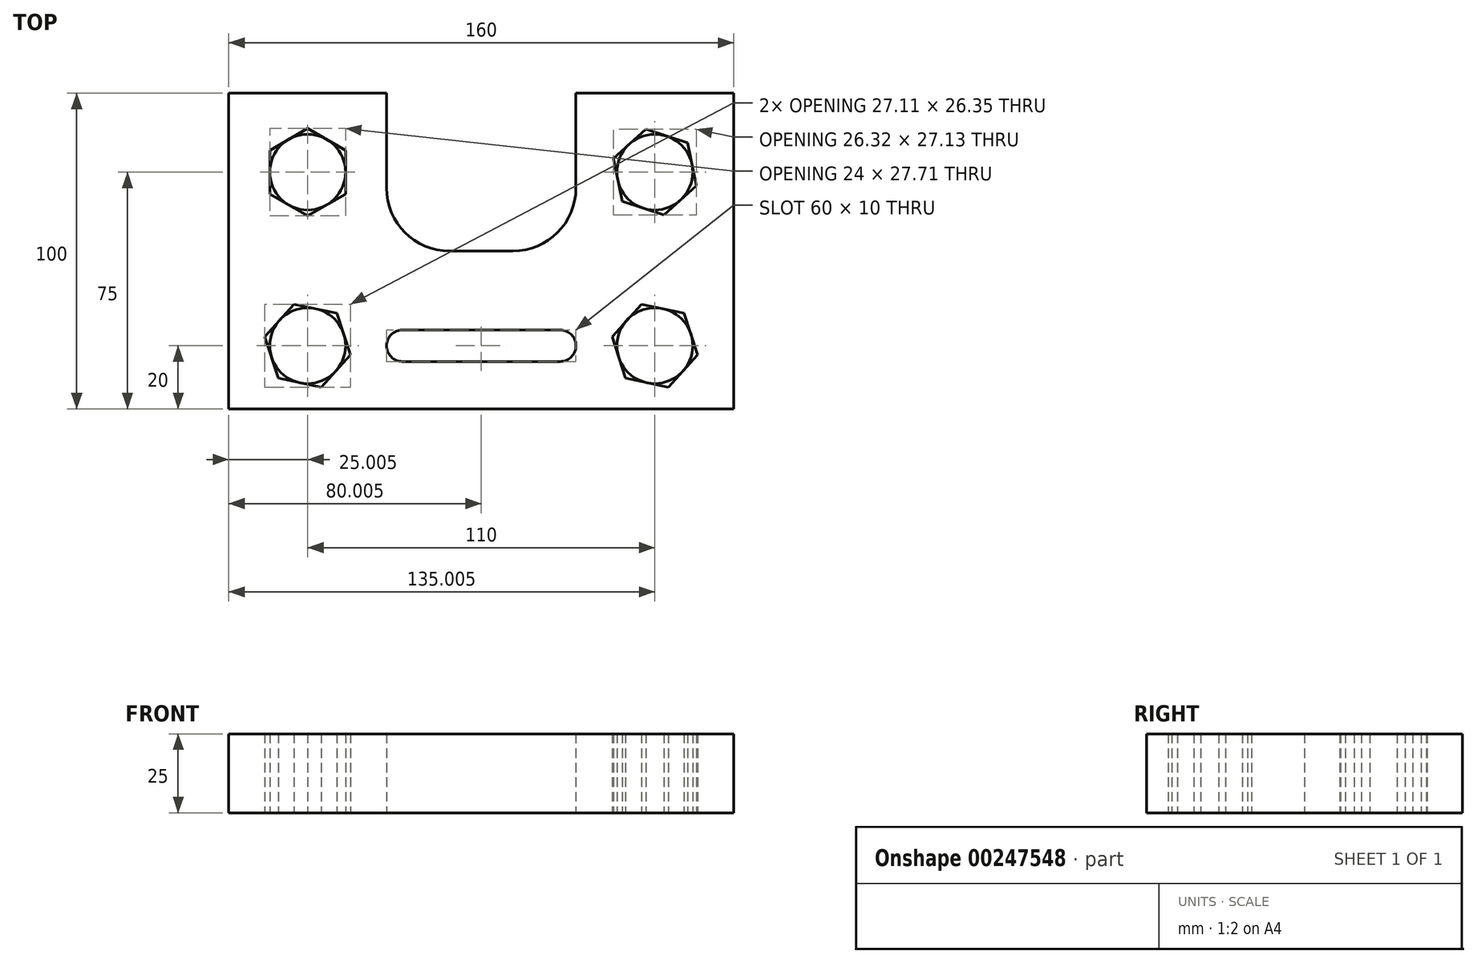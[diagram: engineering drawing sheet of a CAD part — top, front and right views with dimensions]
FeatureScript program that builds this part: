
annotation { "Feature Type Name" : "Feature", "Feature Type Description" : "" }
export const myFeature = defineFeature(function(context is Context, id is Id, definition is map)
    precondition{}
    {
        {
            var Q0;
            Q0=qCreatedBy(makeId("Top.planeOp"),FACE);
            var sketch = newSketch(context, id + "F0", { "sketchPlane" : qUnion([Q0])});
            skLineSegment(sketch, "E0", {"start": v(-28.5, -50) * mm, "end": v(21.5, -50) * mm});
            skLineSegment(sketch, "E1", {"start": v(21.5, -50) * mm, "end": v(51.5, -50) * mm});
            skLineSegment(sketch, "E2", {"start": v(51.5, -50) * mm, "end": v(76.5, -50) * mm});
            skLineSegment(sketch, "E3", {"start": v(76.5, -50) * mm, "end": v(76.5, -30) * mm});
            skLineSegment(sketch, "E4", {"start": v(76.5, -30) * mm, "end": v(76.5, 25) * mm});
            skLineSegment(sketch, "E5", {"start": v(76.5, 25) * mm, "end": v(76.5, 50) * mm});
            skLineSegment(sketch, "E6", {"start": v(76.5, 50) * mm, "end": v(26.5, 50) * mm});
            skLineSegment(sketch, "E7", {"start": v(26.5, 50) * mm, "end": v(26.5, 20) * mm});
            skLineSegment(sketch, "E8", {"start": v(6.5, 0) * mm, "end": v(-13.5, 0) * mm});
            skLineSegment(sketch, "E9", {"start": v(-33.5, 20) * mm, "end": v(-33.5, 50) * mm});
            skLineSegment(sketch, "E10", {"start": v(-33.5, 50) * mm, "end": v(-83.5, 50) * mm});
            skLineSegment(sketch, "E11", {"start": v(-83.5, -50) * mm, "end": v(-83.5, -30) * mm});
            skLineSegment(sketch, "E12", {"start": v(-83.5, -30) * mm, "end": v(-83.5, 25) * mm});
            skLineSegment(sketch, "E13", {"start": v(-83.5, 25) * mm, "end": v(-83.5, 50) * mm});
            skPoint(sketch, "E14", {"position": v(51.5, -30) * mm});
            skPoint(sketch, "E15", {"position": v(51.5, 25) * mm});
            skLineSegment(sketch, "E16", {"start": v(-83.5, -50) * mm, "end": v(-58.5, -50) * mm});
            skLineSegment(sketch, "E17", {"start": v(-58.5, -50) * mm, "end": v(-28.5, -50) * mm});
            skPoint(sketch, "E18", {"position": v(-58.5, -30) * mm});
            skPoint(sketch, "E19", {"position": v(-58.5, 25) * mm});
            skCircle(sketch, "E20", {"center": v(-58.5, 25) * mm, "radius": 12 * mm});
            skCircle(sketch, "E21", {"center": v(-58.5, -30) * mm, "radius": 12 * mm});
            skCircle(sketch, "E22", {"center": v(51.5, -30) * mm, "radius": 12 * mm});
            skCircle(sketch, "E23", {"center": v(51.5, 25) * mm, "radius": 12 * mm});
            skPoint(sketch, "E24.visualSharp", {"position": v(-33.5, 0) * mm});
            skArc(sketch, "E24.filletArc", {"start": v(-33.5, 20) * mm, "mid": v(-27.65, 5.86) * mm, "end": v(-13.5, 0) * mm});
            skPoint(sketch, "E25.visualSharp", {"position": v(26.5, 0) * mm});
            skArc(sketch, "E25.filletArc", {"start": v(6.5, 0) * mm, "mid": v(20.64, 5.86) * mm, "end": v(26.5, 20) * mm});
            skCircle(sketch, "E26.cCircle", {"center": v(-58.5, 25) * mm, "radius": 12 * mm, "construction": true});
            skLineSegment(sketch, "E26.0", {"start": v(-46.5, 31.93) * mm, "end": v(-46.5, 18.07) * mm});
            skLineSegment(sketch, "E26.1", {"start": v(-46.5, 18.07) * mm, "end": v(-58.5, 11.14) * mm});
            skLineSegment(sketch, "E26.2", {"start": v(-58.5, 11.14) * mm, "end": v(-70.5, 18.07) * mm});
            skLineSegment(sketch, "E26.3", {"start": v(-70.5, 18.07) * mm, "end": v(-70.5, 31.93) * mm});
            skLineSegment(sketch, "E26.4", {"start": v(-70.5, 31.93) * mm, "end": v(-58.5, 38.86) * mm});
            skLineSegment(sketch, "E26.5", {"start": v(-58.5, 38.86) * mm, "end": v(-46.5, 31.93) * mm});
            skPoint(sketch, "E26.0.midPoint", {"position": v(-46.5, 25) * mm});
            skCircle(sketch, "E27.cCircle", {"center": v(-58.5, -30) * mm, "radius": 12 * mm, "construction": true});
            skLineSegment(sketch, "E27.0", {"start": v(-49.24, -19.7) * mm, "end": v(-44.95, -32.87) * mm});
            skLineSegment(sketch, "E27.1", {"start": v(-44.95, -32.87) * mm, "end": v(-54.21, -43.17) * mm});
            skLineSegment(sketch, "E27.2", {"start": v(-54.21, -43.17) * mm, "end": v(-67.77, -40.3) * mm});
            skLineSegment(sketch, "E27.3", {"start": v(-67.77, -40.3) * mm, "end": v(-72.06, -27.13) * mm});
            skLineSegment(sketch, "E27.4", {"start": v(-72.06, -27.13) * mm, "end": v(-62.8, -16.83) * mm});
            skLineSegment(sketch, "E27.5", {"start": v(-62.8, -16.83) * mm, "end": v(-49.24, -19.7) * mm});
            skPoint(sketch, "E27.0.midPoint", {"position": v(-47.1, -26.28) * mm});
            skCircle(sketch, "E28.cCircle", {"center": v(51.5, -30) * mm, "radius": 12 * mm, "construction": true});
            skLineSegment(sketch, "E28.0", {"start": v(60.76, -19.7) * mm, "end": v(65.05, -32.87) * mm});
            skLineSegment(sketch, "E28.1", {"start": v(65.05, -32.87) * mm, "end": v(55.79, -43.17) * mm});
            skLineSegment(sketch, "E28.2", {"start": v(55.79, -43.17) * mm, "end": v(42.23, -40.3) * mm});
            skLineSegment(sketch, "E28.3", {"start": v(42.23, -40.3) * mm, "end": v(37.94, -27.13) * mm});
            skLineSegment(sketch, "E28.4", {"start": v(37.94, -27.13) * mm, "end": v(47.2, -16.83) * mm});
            skLineSegment(sketch, "E28.5", {"start": v(47.2, -16.83) * mm, "end": v(60.76, -19.7) * mm});
            skPoint(sketch, "E28.0.midPoint", {"position": v(62.9, -26.28) * mm});
            skCircle(sketch, "E29.cCircle", {"center": v(51.5, 25) * mm, "radius": 12 * mm, "construction": true});
            skLineSegment(sketch, "E29.0", {"start": v(61.83, 34.23) * mm, "end": v(64.66, 20.67) * mm});
            skLineSegment(sketch, "E29.1", {"start": v(64.66, 20.67) * mm, "end": v(54.33, 11.44) * mm});
            skLineSegment(sketch, "E29.2", {"start": v(54.33, 11.44) * mm, "end": v(41.16, 15.77) * mm});
            skLineSegment(sketch, "E29.3", {"start": v(41.16, 15.77) * mm, "end": v(38.33, 29.33) * mm});
            skLineSegment(sketch, "E29.4", {"start": v(38.33, 29.33) * mm, "end": v(48.66, 38.56) * mm});
            skLineSegment(sketch, "E29.5", {"start": v(48.66, 38.56) * mm, "end": v(61.83, 34.23) * mm});
            skPoint(sketch, "E29.0.midPoint", {"position": v(63.24, 27.45) * mm});
            skPoint(sketch, "E30", {"position": v(21.5, -30) * mm});
            skPoint(sketch, "E31", {"position": v(-28.5, -30) * mm});
            skArc(sketch, "E32", {"start": v(21.5, -35) * mm, "mid": v(26.5, -30) * mm, "end": v(21.5, -25) * mm});
            skArc(sketch, "E33", {"start": v(-28.5, -25) * mm, "mid": v(-33.5, -30) * mm, "end": v(-28.5, -35) * mm});
            skLineSegment(sketch, "E34", {"start": v(-28.5, -25) * mm, "end": v(21.5, -25) * mm});
            skLineSegment(sketch, "E35", {"start": v(-28.5, -35) * mm, "end": v(21.5, -35) * mm});
            skSolve(sketch);
        }
        {
            var Q0;
            Q0=makeQuery(id+"F0.imprint","IMPRINT",FACE,{"disambiguationData":[TD([[makeQuery(id+"F0.imprint","IMPRINT",EDGE,{"derivedFrom":sQuery(id+"F0.wireOp",EDGE,"E0")}),1.0]])]});
            var Q1;
            {var subQ0=sQuery(id+"F0.wireOp",EDGE,"E20");var subQ4=makeQuery(id+"F0.imprint","INTERSECT",VERTEX,{"derivedFrom":[subQ0,sQuery(id+"F0.wireOp",EDGE,"E26.5")]});Q1=makeQuery(id+"F0.imprint","IMPRINT",FACE,{"disambiguationData":[TD([[makeQuery(id+"F0.imprint","IMPRINT",EDGE,{"disambiguationData":[TD([[subQ4,1.0]])],"derivedFrom":subQ0}),1.0]])]});}
            var Q2;
            {var subQ0=sQuery(id+"F0.wireOp",EDGE,"E21");var subQ4=makeQuery(id+"F0.imprint","INTERSECT",VERTEX,{"derivedFrom":[subQ0,sQuery(id+"F0.wireOp",EDGE,"E27.5")]});Q2=makeQuery(id+"F0.imprint","IMPRINT",FACE,{"disambiguationData":[TD([[makeQuery(id+"F0.imprint","IMPRINT",EDGE,{"disambiguationData":[TD([[subQ4,1.0]])],"derivedFrom":subQ0}),1.0]])]});}
            var Q3;
            {var subQ0=sQuery(id+"F0.wireOp",EDGE,"E22");var subQ4=makeQuery(id+"F0.imprint","INTERSECT",VERTEX,{"derivedFrom":[subQ0,sQuery(id+"F0.wireOp",EDGE,"E28.5")]});Q3=makeQuery(id+"F0.imprint","IMPRINT",FACE,{"disambiguationData":[TD([[makeQuery(id+"F0.imprint","IMPRINT",EDGE,{"disambiguationData":[TD([[subQ4,1.0]])],"derivedFrom":subQ0}),1.0]])]});}
            var Q4;
            {var subQ0=sQuery(id+"F0.wireOp",EDGE,"E23");var subQ5=makeQuery(id+"F0.imprint","INTERSECT",VERTEX,{"derivedFrom":[subQ0,sQuery(id+"F0.wireOp",EDGE,"E29.5")]});Q4=makeQuery(id+"F0.imprint","IMPRINT",FACE,{"disambiguationData":[TD([[makeQuery(id+"F0.imprint","IMPRINT",EDGE,{"disambiguationData":[TD([[subQ5,1.0]])],"derivedFrom":subQ0}),1.0]])]});}
            extrude(context, id + "F1", {"entities" : qUnion([Q0, Q1, Q2, Q3, Q4]), "depth" : 25 * mm});
        }
    });
